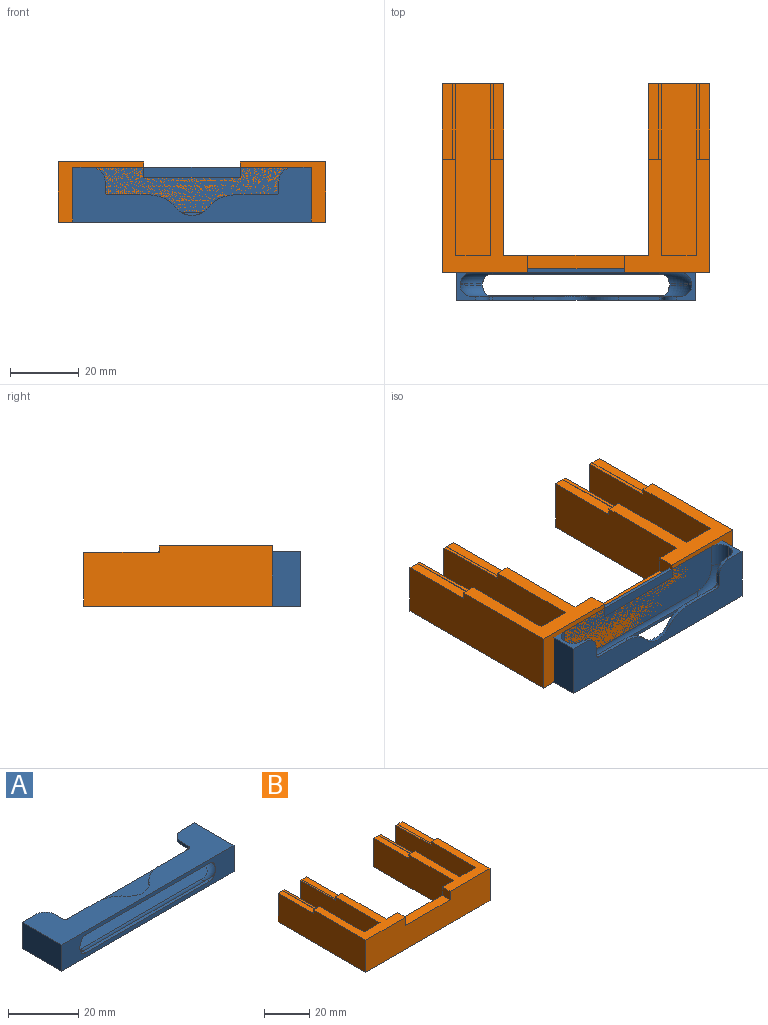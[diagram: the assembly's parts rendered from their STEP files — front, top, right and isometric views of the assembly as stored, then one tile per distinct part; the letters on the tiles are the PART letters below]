
ASSEMBLY  parts=2 mates=2
PART A: 44 faces, bbox 69.5x17.2x9.1 mm
  f0: plane 15.9x9.1mm, normal (-1,0,0), area 144.7mm2, adj f4,f8,f36,f43
  f1: cylinder r=9.4mm len=8.9mm, axis (0,0,1), area 3.5mm2, adj f2,f5,f23,f43
  f2: torus R=6mm, axis (0,0,1), area 59.9mm2, adj f1,f12,f14,f15,f19,f24,f25,f43
  f3: torus R=6mm, axis (0,0,1), area 59.9mm2, adj f7,f15,f16,f17,f19,f20,f33,f43
  f4: plane 69.5x15.9mm, normal (0,0,1), area 625.4mm2, adj f0,f21,f26,f27,f29,f30,f34,f35
  f5: torus R=6mm, axis (0,0,1), area 59.7mm2, adj f1,f10,f11,f13,f22,f28,f37,f43
  f6: torus R=6mm, axis (0,0,1), area 59.7mm2, adj f7,f9,f10,f18,f28,f31,f37,f43
  f7: cylinder r=9.4mm len=8.9mm, axis (0,0,1), area 3.5mm2, adj f3,f6,f32,f43
  f8: plane 69.5x15.9mm, normal (0,0,-1), area 1105mm2, adj f0,f35,f36,f43
  f9: cylinder r=2mm len=2mm, axis (0,1,0), area 2mm2, adj f6,f10,f18,f43
  f10: plane 50x1.15mm, normal (0,0,1), area 56.3mm2, adj f5,f6,f9,f11,f28,f43
  f11: cylinder r=2mm len=2mm, axis (0,1,0), area 2mm2, adj f5,f10,f13,f43
  f12: plane 0.23x0.07mm, normal (1,0,0), area 0mm2, adj f2,f14,f43
  f13: plane 0.03x0.01mm, normal (1,0,0), area 0mm2, adj f5,f11,f43
  f14: cylinder r=2mm len=2mm, axis (0,1,0), area 2.7mm2, adj f2,f12,f15,f43
  f15: plane 50x1.53mm, normal (0,0,-1), area 75.2mm2, adj f2,f3,f14,f16,f19,f43
  f16: cylinder r=2mm len=2mm, axis (0,1,0), area 2.7mm2, adj f3,f15,f17,f43
  f17: plane 0.23x0.07mm, normal (-1,0,0), area 0mm2, adj f3,f16,f43
  f18: plane 0.03x0.01mm, normal (-1,0,0), area 0mm2, adj f6,f9,f43
  f19: cylinder r=3.4mm len=48.7mm, axis (1,0,0), area 65.5mm2, adj f2,f3,f15,f20,f25,f40
  f20: plane 27.03x13mm, normal (0,0,-1), area 149.3mm2, adj f3,f19,f29,f30,f33,f34,f36,f38
  f21: plane 11.86x1mm, normal (0,1,0), area 11.9mm2, adj f4,f25,f27,f41
  f22: cylinder r=3.4mm len=7mm, axis (0,-1,0), area 37mm2, adj f5,f23,f36,f37
  f23: plane 7x0.3mm, normal (1,0,0), area 2.1mm2, adj f1,f22,f24,f36
  f24: cylinder r=3.4mm len=7mm, axis (0,-1,0), area 37.7mm2, adj f2,f23,f25,f36
  f25: plane 27.03x13mm, normal (0,0,-1), area 149.3mm2, adj f2,f19,f21,f24,f26,f27,f36,f39
  f26: plane 3x1mm, normal (1,0,0), area 3mm2, adj f4,f25,f27,f39
  f27: cylinder r=1mm len=1mm, axis (0,0,1), area 1.6mm2, adj f4,f21,f25,f26
  f28: cylinder r=3.4mm len=48.7mm, axis (1,0,0), area 90.9mm2, adj f5,f6,f10,f37
  f29: plane 11.86x1mm, normal (0,1,0), area 11.9mm2, adj f4,f20,f30,f42
  f30: cylinder r=1mm len=1mm, axis (0,0,1), area 1.6mm2, adj f4,f20,f29,f34
  f31: cylinder r=3.4mm len=7mm, axis (0,1,0), area 37mm2, adj f6,f32,f36,f37
  f32: plane 7x0.3mm, normal (-1,0,0), area 2.1mm2, adj f7,f31,f33,f36
  f33: cylinder r=3.4mm len=7mm, axis (0,1,0), area 37.7mm2, adj f3,f20,f32,f36
  f34: plane 3x1mm, normal (-1,0,0), area 3mm2, adj f4,f20,f30,f38
  f35: plane 15.9x9.1mm, normal (1,0,0), area 144.7mm2, adj f4,f8,f36,f43
  f36: plane 69.5x9.1mm, normal (0,1,0), area 104.4mm2, adj f0,f4,f8,f20,f22,f23,f24,f25
  f37: plane 60.7x13mm, normal (0,0,1), area 773.6mm2, adj f5,f6,f22,f28,f31,f36
  f38: cylinder r=4mm len=4mm, axis (0,0,1), area 6.3mm2, adj f4,f20,f34,f36
  f39: cylinder r=4mm len=4mm, axis (0,0,1), area 6.3mm2, adj f4,f25,f26,f36
  f40: cylinder r=6mm len=9.37mm, axis (0,0,1), area 11.3mm2, adj f4,f19,f20,f25,f41,f42
  f41: cylinder r=10mm len=7.81mm, axis (0,0,1), area 9mm2, adj f4,f21,f25,f40
  f42: cylinder r=10mm len=7.81mm, axis (0,0,1), area 9mm2, adj f4,f20,f29,f40
  f43: plane 69.5x9.1mm, normal (0,-1,0), area 294.6mm2, adj f0,f1,f2,f3,f4,f5,f6,f7
PART B: 38 faces, bbox 78x55x17.5 mm
  f0: plane 22x0.25mm, normal (-1,0,0), area 2.8mm2, adj f4,f10,f16
  f1: plane 18x15.5mm, normal (0,1,0), area 151.5mm2, adj f2,f4,f5,f6,f7,f8,f9,f15
  f2: plane 22x3mm, normal (0,0,1), area 66mm2, adj f1,f3,f5,f11
  f3: plane 4x2mm, normal (0,1,0), area 7.7mm2, adj f2,f5,f6,f11,f15,f36
  f4: plane 22x3mm, normal (0,0,1), area 66mm2, adj f0,f1,f8,f10
  f5: plane 50x17.5mm, normal (1,0,0), area 831mm2, adj f1,f2,f3,f9,f19,f36
  f6: plane 50x14.75mm, normal (-1,0,0), area 696.3mm2, adj f1,f3,f15,f17,f18,f36
  f7: plane 50x14.75mm, normal (1,0,0), area 696.3mm2, adj f1,f10,f16,f17,f18,f36
  f8: plane 55x17.5mm, normal (-1,0,0), area 918.5mm2, adj f1,f4,f9,f10,f14,f36
  f9: plane 78x55mm, normal (0,0,-1), area 2190mm2, adj f1,f5,f8,f14,f19,f21,f25,f28
  f10: plane 4x2mm, normal (0,1,0), area 7.7mm2, adj f0,f4,f7,f8,f16,f36
  f11: plane 22x0.25mm, normal (1,0,0), area 2.8mm2, adj f2,f3,f15
  f12: plane 28x5mm, normal (0,0,1), area 140mm2, adj f13,f14,f19,f31
  f13: plane 5x4.5mm, normal (1,0,0), area 22.5mm2, adj f12,f14,f19,f36
  f14: plane 78x17.5mm, normal (0,-1,0), area 1239mm2, adj f8,f9,f12,f13,f28,f31,f36,f37
  f15: plane 22x1mm, normal (0,0.01,1), area 22mm2, adj f1,f3,f6,f11
  f16: plane 22x1mm, normal (0,0.01,1), area 22mm2, adj f0,f1,f7,f10
  f17: plane 50x10mm, normal (0,0,1), area 500mm2, adj f1,f6,f7,f18
  f18: plane 14.75x10mm, normal (0,1,0), area 147.5mm2, adj f6,f7,f17,f36
  f19: plane 42x17.5mm, normal (0,1,0), area 609mm2, adj f5,f9,f12,f13,f25,f31,f36,f37
  f20: plane 22x0.25mm, normal (1,0,0), area 2.8mm2, adj f24,f29,f33
  f21: plane 18x15.5mm, normal (0,1,0), area 151.5mm2, adj f9,f22,f24,f25,f26,f27,f28,f32
  f22: plane 22x3mm, normal (0,0,1), area 66mm2, adj f21,f23,f25,f30
  f23: plane 4x2mm, normal (0,1,0), area 7.7mm2, adj f22,f25,f26,f30,f32,f37
  f24: plane 22x3mm, normal (0,0,1), area 66mm2, adj f20,f21,f28,f29
  f25: plane 50x17.5mm, normal (-1,0,0), area 831mm2, adj f9,f19,f21,f22,f23,f37
  f26: plane 50x14.75mm, normal (1,0,0), area 696.3mm2, adj f21,f23,f32,f34,f35,f37
  f27: plane 50x14.75mm, normal (-1,0,0), area 696.3mm2, adj f21,f29,f33,f34,f35,f37
  f28: plane 55x17.5mm, normal (1,0,0), area 918.5mm2, adj f9,f14,f21,f24,f29,f37
  f29: plane 4x2mm, normal (0,1,0), area 7.7mm2, adj f20,f24,f27,f28,f33,f37
  f30: plane 22x0.25mm, normal (-1,0,0), area 2.8mm2, adj f22,f23,f32
  f31: plane 5x4.5mm, normal (-1,0,0), area 22.5mm2, adj f12,f14,f19,f37
  f32: plane 22x1mm, normal (0,0.01,1), area 22mm2, adj f21,f23,f26,f30
  f33: plane 22x1mm, normal (0,0.01,1), area 22mm2, adj f20,f21,f27,f29
  f34: plane 50x10mm, normal (0,0,1), area 500mm2, adj f21,f26,f27,f35
  f35: plane 14.75x10mm, normal (0,1,0), area 147.5mm2, adj f26,f27,f34,f37
  f36: plane 33x25mm, normal (0,0,1), area 349mm2, adj f3,f5,f6,f7,f8,f10,f13,f14
  f37: plane 33x25mm, normal (0,0,1), area 349mm2, adj f14,f19,f23,f25,f26,f27,f28,f29
PLACE A rot(axis=(1,0,0),90deg) t=(3.54,-18.49,0.1)mm
PLACE B t=(3.54,-4.49,4.95)mm fixed
MATE planar A.f43 <-> B.f9  axis (0,0,-1) through (3.54,-22.92,-2.8)mm
MATE planar A.f37 <-> B.f14  axis (0,-1,0) through (3.54,-19.49,6.71)mm
